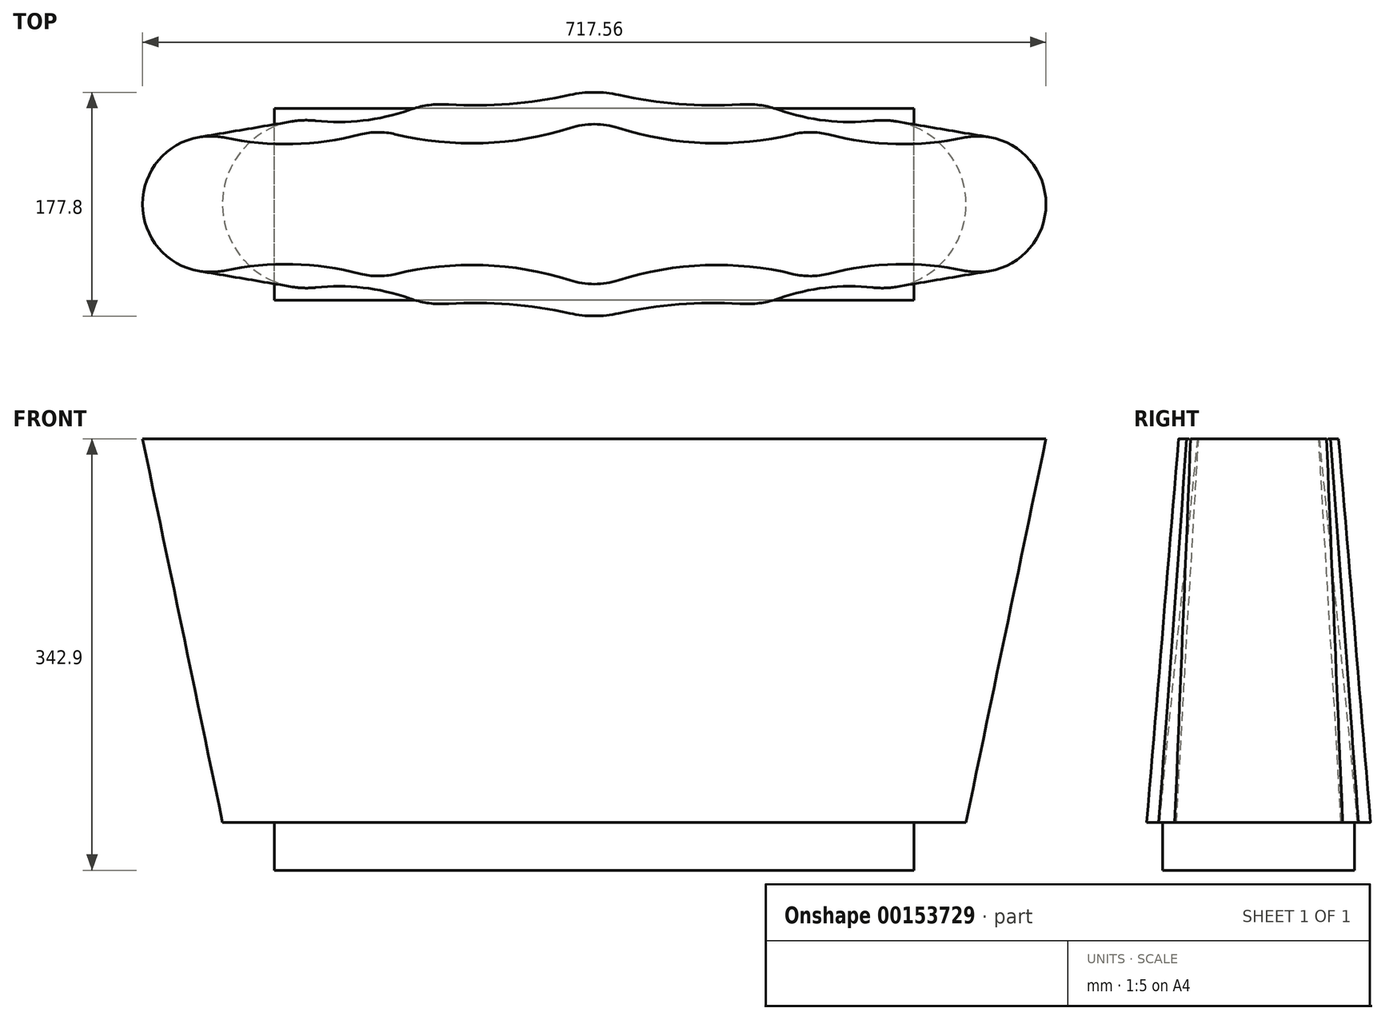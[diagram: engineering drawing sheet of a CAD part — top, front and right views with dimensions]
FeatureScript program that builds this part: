
annotation { "Feature Type Name" : "Feature", "Feature Type Description" : "" }
export const myFeature = defineFeature(function(context is Context, id is Id, definition is map)
    precondition{}
    {
        {
            var Q0;
            Q0=qCreatedBy(makeId("Top.planeOp"),FACE);
            var sketch = newSketch(context, id + "F0", { "sketchPlane" : qUnion([Q0])});
            skLineSegment(sketch, "E0.bottom", {"start": v(254, -76.2) * mm, "end": v(-254, -76.2) * mm});
            skLineSegment(sketch, "E0.top", {"start": v(254, 76.2) * mm, "end": v(-254, 76.2) * mm});
            skLineSegment(sketch, "E0.left", {"start": v(254, -76.2) * mm, "end": v(254, 76.2) * mm});
            skLineSegment(sketch, "E0.right", {"start": v(-254, -76.2) * mm, "end": v(-254, 76.2) * mm});
            skPoint(sketch, "E0.middle", {"position": v(0, 0) * mm});
            skSolve(sketch);
        }
        {
            var Q0;
            Q0=makeQuery(id+"F0.imprint","IMPRINT",FACE,{"disambiguationData":[TD([[makeQuery(id+"F0.imprint","IMPRINT",EDGE,{"derivedFrom":sQuery(id+"F0.wireOp",EDGE,"E0.bottom")}),-1.0]])]});
            extrude(context, id + "F1", {"entities" : qUnion([Q0]), "depth" : 38.1 * mm});
        }
        {
            var Q0;
            Q0=makeQuery(id+"F1.opExtrude","CAP_FACE",FACE,{"disambiguationData":[OSD([sQuery(id+"F0.wireOp",EDGE,"E0.bottom"),sQuery(id+"F0.wireOp",EDGE,"E0.top"),sQuery(id+"F0.wireOp",EDGE,"E0.left"),sQuery(id+"F0.wireOp",EDGE,"E0.right")])],"isStart":false});
            var sketch = newSketch(context, id + "F2", { "sketchPlane" : qUnion([Q0])});
            skArc(sketch, "E1", {"start": v(-19.34, -86.77) * mm, "mid": v(0, -88.9) * mm, "end": v(19.34, -86.77) * mm});
            skPoint(sketch, "E2.centerSnap0", {"position": v(254, 0) * mm});
            skPoint(sketch, "E3.MirrorP", {"position": v(-254, 0) * mm});
            skArc(sketch, "E4.MirrorC", {"start": v(-221.27, -66.27) * mm, "mid": v(-295.28, 0) * mm, "end": v(-221.27, 66.27) * mm});
            skArc(sketch, "E5.MirrorC", {"start": v(-147.12, 74.83) * mm, "mid": v(-131.62, 78.61) * mm, "end": v(-115.67, 79.22) * mm});
            skArc(sketch, "E6", {"start": v(-115.67, 79.22) * mm, "mid": v(-67.24, 79.6) * mm, "end": v(-19.34, 86.77) * mm});
            skArc(sketch, "E7", {"start": v(-221.27, 66.27) * mm, "mid": v(-183.71, 66.36) * mm, "end": v(-147.12, 74.83) * mm});
            skArc(sketch, "E8.MirrorCS", {"start": v(-115.67, -79.22) * mm, "mid": v(-67.24, -79.6) * mm, "end": v(-19.34, -86.77) * mm});
            skArc(sketch, "E9.MirrorCS", {"start": v(-221.27, -66.27) * mm, "mid": v(-183.71, -66.36) * mm, "end": v(-147.12, -74.83) * mm});
            skArc(sketch, "E10.trimOffspring", {"start": v(-115.67, -79.22) * mm, "mid": v(-131.62, -78.61) * mm, "end": v(-147.12, -74.83) * mm});
            skArc(sketch, "E11.MirrorCS", {"start": v(115.67, 79.22) * mm, "mid": v(67.24, 79.6) * mm, "end": v(19.34, 86.77) * mm});
            skArc(sketch, "E12.MirrorCS", {"start": v(147.12, 74.83) * mm, "mid": v(131.62, 78.61) * mm, "end": v(115.67, 79.22) * mm});
            skArc(sketch, "E13.MirrorCS", {"start": v(221.27, 66.27) * mm, "mid": v(183.71, 66.36) * mm, "end": v(147.12, 74.83) * mm});
            skArc(sketch, "E14.MirrorCS", {"start": v(221.27, -66.27) * mm, "mid": v(295.28, 0) * mm, "end": v(221.27, 66.27) * mm});
            skArc(sketch, "E15.MirrorCS", {"start": v(221.27, -66.27) * mm, "mid": v(183.71, -66.36) * mm, "end": v(147.12, -74.83) * mm});
            skArc(sketch, "E16.MirrorCS", {"start": v(115.67, -79.22) * mm, "mid": v(131.62, -78.61) * mm, "end": v(147.12, -74.83) * mm});
            skArc(sketch, "E17.MirrorCS", {"start": v(115.67, -79.22) * mm, "mid": v(67.24, -79.6) * mm, "end": v(19.34, -86.77) * mm});
            skArc(sketch, "E18.trimOffspring", {"start": v(19.34, 86.77) * mm, "mid": v(0, 88.9) * mm, "end": v(-19.34, 86.77) * mm});
            skSolve(sketch);
        }
        {
            var Q0;
            {var subQ0=sQuery(id+"F2.wireOp",EDGE,"4XwoblfJ-CLJp-xlPN-5V5L-qZCIPSraK3I2");var subQ1=sQuery(id+"F2.wireOp",EDGE,"E1");var subQ8=makeQuery(id+"F2.imprint","INTERSECT",VERTEX,{"disambiguationData":[OD(0.0)],"derivedFrom":[subQ1,subQ0]});Q0=makeQuery(id+"F2.imprint","IMPRINT",FACE,{"disambiguationData":[TD([[makeQuery(id+"F2.imprint","IMPRINT",EDGE,{"disambiguationData":[TD([[subQ8,-1.0]])],"derivedFrom":subQ1}),1.0]])]});}
            cPlane(context, id + "F3", {"entities" : qUnion([Q0]), "cplaneType" : CPlaneType.OFFSET, "offset" : 304.8 * mm, "width" : 152.4 * mm, "height" : 152.4 * mm});
        }
        {
            var Q0;
            Q0=qCreatedBy(id+"F3.planeOp",FACE);
            var sketch = newSketch(context, id + "F4", { "sketchPlane" : qUnion([Q0])});
            skArc(sketch, "E19", {"start": v(-19.26, -60.5) * mm, "mid": v(0, -63.5) * mm, "end": v(19.26, -60.5) * mm});
            skArc(sketch, "E20", {"start": v(-185.88, -55.3) * mm, "mid": v(-171.97, -57.15) * mm, "end": v(-158.04, -55.55) * mm});
            skArc(sketch, "E21", {"start": v(-293.6, 52.8) * mm, "mid": v(-358.78, 0) * mm, "end": v(-293.6, -52.8) * mm});
            skCircle(sketch, "E22.0", {"center": v(-120.65, 0) * mm, "radius": 79.38 * mm, "construction": true});
            skArc(sketch, "E23.0", {"start": v(-189.7, -54.16) * mm, "mid": v(-295.28, 0) * mm, "end": v(-189.7, 54.16) * mm, "construction": true});
            skArc(sketch, "E24", {"start": v(-293.6, 52.8) * mm, "mid": v(-239.6, 47.77) * mm, "end": v(-185.88, 55.3) * mm});
            skArc(sketch, "E25", {"start": v(-158.04, 55.55) * mm, "mid": v(-88.31, 48.52) * mm, "end": v(-19.26, 60.5) * mm});
            skArc(sketch, "E26.MirrorCS", {"start": v(-293.6, -52.8) * mm, "mid": v(-239.6, -47.77) * mm, "end": v(-185.88, -55.3) * mm});
            skArc(sketch, "E27.MirrorCS", {"start": v(-158.04, -55.55) * mm, "mid": v(-88.31, -48.52) * mm, "end": v(-19.26, -60.5) * mm});
            skArc(sketch, "E28.trimOffspring", {"start": v(-158.04, 55.55) * mm, "mid": v(-171.97, 57.15) * mm, "end": v(-185.88, 55.3) * mm});
            skArc(sketch, "E29.MirrorCS", {"start": v(158.04, 55.55) * mm, "mid": v(88.31, 48.52) * mm, "end": v(19.26, 60.5) * mm});
            skArc(sketch, "E30.MirrorCS", {"start": v(158.04, 55.55) * mm, "mid": v(171.97, 57.15) * mm, "end": v(185.88, 55.3) * mm});
            skArc(sketch, "E31.MirrorCS", {"start": v(293.6, 52.8) * mm, "mid": v(239.6, 47.77) * mm, "end": v(185.88, 55.3) * mm});
            skArc(sketch, "E32.MirrorCS", {"start": v(293.6, 52.8) * mm, "mid": v(358.78, 0) * mm, "end": v(293.6, -52.8) * mm});
            skArc(sketch, "E33.MirrorCS", {"start": v(293.6, -52.8) * mm, "mid": v(239.6, -47.77) * mm, "end": v(185.88, -55.3) * mm});
            skArc(sketch, "E34.MirrorCS", {"start": v(185.88, -55.3) * mm, "mid": v(171.97, -57.15) * mm, "end": v(158.04, -55.55) * mm});
            skArc(sketch, "E35.MirrorCS", {"start": v(158.04, -55.55) * mm, "mid": v(88.31, -48.52) * mm, "end": v(19.26, -60.5) * mm});
            skArc(sketch, "E36.trimOffspring", {"start": v(19.26, 60.5) * mm, "mid": v(0, 63.5) * mm, "end": v(-19.26, 60.5) * mm});
            skSolve(sketch);
        }
        {
            var Q0;
            Q0 = qSketchRegion(id + "F2", true);
            var Q1;
            Q1 = qSketchRegion(id + "F4", true);
            loft(context, id + "F5", {"operationType" : NewBodyOperationType.ADD, "sheetProfilesArray" : [{ "sheetProfileEntities" : qUnion([Q0]) }, { "sheetProfileEntities" : qUnion([Q1]) }]});
        }
    });
